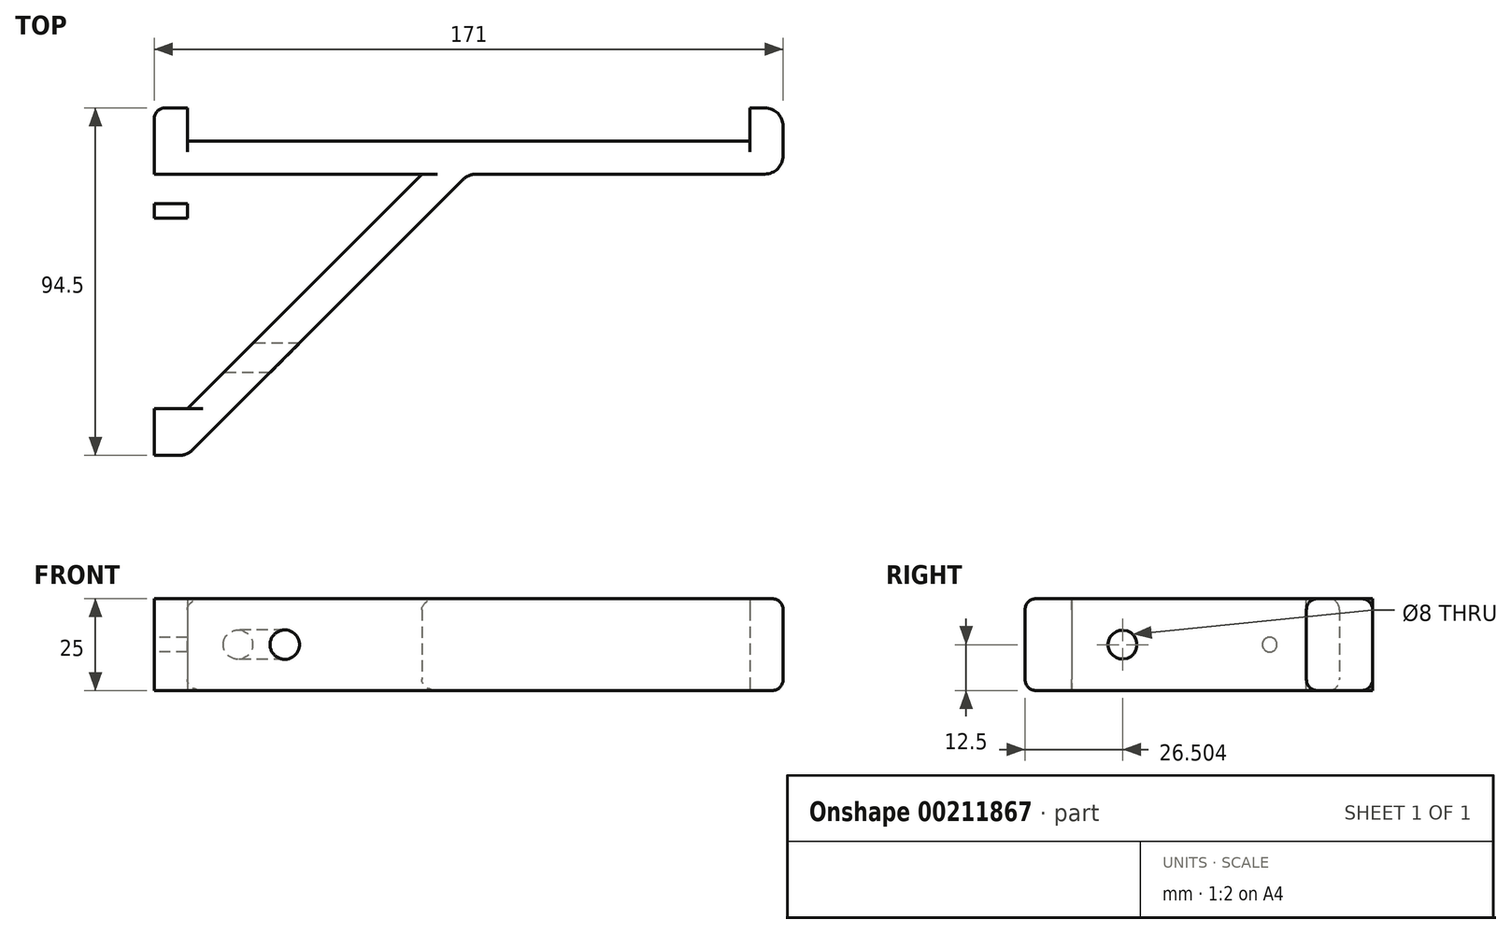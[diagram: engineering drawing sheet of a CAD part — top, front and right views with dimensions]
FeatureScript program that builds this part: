
annotation { "Feature Type Name" : "Feature", "Feature Type Description" : "" }
export const myFeature = defineFeature(function(context is Context, id is Id, definition is map)
    precondition{}
    {
        {
            var Q0;
            Q0=qCreatedBy(makeId("Top.planeOp"),FACE);
            var sketch = newSketch(context, id + "F0", { "sketchPlane" : qUnion([Q0])});
            skLineSegment(sketch, "E0.bottom", {"start": v(-148.67, 15.26) * mm, "end": v(4.33, 15.26) * mm});
            skLineSegment(sketch, "E0.top", {"start": v(-148.67, 24.26) * mm, "end": v(4.33, 24.26) * mm});
            skLineSegment(sketch, "E0.left", {"start": v(-148.67, 15.26) * mm, "end": v(-148.67, 24.26) * mm});
            skLineSegment(sketch, "E0.right", {"start": v(4.33, 15.26) * mm, "end": v(4.33, 24.26) * mm});
            skLineSegment(sketch, "E1.bottom", {"start": v(-148.67, 15.26) * mm, "end": v(-157.67, 15.26) * mm});
            skLineSegment(sketch, "E1.top", {"start": v(-148.67, -61.24) * mm, "end": v(-157.67, -61.24) * mm});
            skLineSegment(sketch, "E1.left", {"start": v(-148.67, -61.24) * mm, "end": v(-148.67, -61.24) * mm});
            skLineSegment(sketch, "E1.right", {"start": v(-157.67, 15.26) * mm, "end": v(-157.67, -61.24) * mm});
            skLineSegment(sketch, "E2", {"start": v(-72.17, 15.26) * mm, "end": v(-72.17, 15.26) * mm});
            skPoint(sketch, "E3.visualSharp", {"position": v(-148.67, 15.26) * mm});
            skLineSegment(sketch, "E4.bottom", {"start": v(-157.67, 15.26) * mm, "end": v(-148.67, 15.26) * mm});
            skLineSegment(sketch, "E4.top", {"start": v(-157.67, 24.26) * mm, "end": v(-148.67, 24.26) * mm});
            skLineSegment(sketch, "E4.left", {"start": v(-157.67, 15.26) * mm, "end": v(-157.67, 24.26) * mm});
            skLineSegment(sketch, "E5", {"start": v(-148.67, 15.26) * mm, "end": v(-148.67, -61.24) * mm});
            skLineSegment(sketch, "E6.bottom", {"start": v(4.33, 15.26) * mm, "end": v(13.33, 15.26) * mm});
            skLineSegment(sketch, "E6.top", {"start": v(4.33, 33.26) * mm, "end": v(13.33, 33.26) * mm});
            skLineSegment(sketch, "E6.left", {"start": v(4.33, 15.26) * mm, "end": v(4.33, 33.26) * mm});
            skLineSegment(sketch, "E6.right", {"start": v(13.33, 15.26) * mm, "end": v(13.33, 33.26) * mm});
            skLineSegment(sketch, "E7.top", {"start": v(-157.67, 33.26) * mm, "end": v(-148.67, 33.26) * mm});
            skLineSegment(sketch, "E7.left", {"start": v(-157.67, 24.26) * mm, "end": v(-157.67, 33.26) * mm});
            skLineSegment(sketch, "E7.right", {"start": v(-148.67, 24.26) * mm, "end": v(-148.67, 33.26) * mm});
            skLineSegment(sketch, "E8", {"start": v(-148.67, -61.24) * mm, "end": v(-72.17, 15.26) * mm});
            skLineSegment(sketch, "E9", {"start": v(-110.42, -22.99) * mm, "end": v(-116.78, -16.62) * mm});
            skLineSegment(sketch, "E10", {"start": v(-116.78, -16.62) * mm, "end": v(-148.67, -48.5) * mm});
            skLineSegment(sketch, "E11", {"start": v(-148.67, -48.5) * mm, "end": v(-116.78, -16.62) * mm});
            skLineSegment(sketch, "E12", {"start": v(-116.78, -16.62) * mm, "end": v(-84.9, 15.26) * mm});
            skSolve(sketch);
        }
        {
            var Q0;
            Q0 = qSketchRegion(id + "F0", true);
            extrude(context, id + "F1", {"entities" : qUnion([Q0]), "depth" : 25 * mm});
        }
        {
            var Q0;
            Q0=makeQuery(id+"F1.opExtrude","SWEPT_FACE",FACE,{"disambiguationData":[OSD([sQuery(id+"F0.wireOp",EDGE,"E1.right"),sQuery(id+"F0.wireOp",EDGE,"E4.left"),sQuery(id+"F0.wireOp",EDGE,"E7.left")])]});
            var sketch = newSketch(context, id + "F2", { "sketchPlane" : qUnion([Q0])});
            skLineSegment(sketch, "E13.0", {"start": v(-15.26, 25) * mm, "end": v(-15.26, 0) * mm});
            skLineSegment(sketch, "E13.1", {"start": v(48.5, 25) * mm, "end": v(48.5, 0) * mm});
            skLineSegment(sketch, "E14", {"start": v(-15.26, 12.5) * mm, "end": v(48.5, 12.5) * mm});
            skCircle(sketch, "E15", {"center": v(-5.26, 12.5) * mm, "radius": 2 * mm});
            skCircle(sketch, "E16", {"center": v(34.74, 12.5) * mm, "radius": 2 * mm});
            skSolve(sketch);
        }
        {
            var Q0;
            {var subQ0=sQuery(id+"F2.wireOp",EDGE,"E15");var subQ1=sQuery(id+"F2.wireOp",EDGE,"E14");var subQ2=makeQuery(id+"F2.imprint","INTERSECT",VERTEX,{"disambiguationData":[OD(0.0)],"derivedFrom":[subQ1,subQ0]});Q0=makeQuery(id+"F2.imprint","IMPRINT",FACE,{"disambiguationData":[TD([[makeQuery(id+"F2.imprint","IMPRINT",EDGE,{"disambiguationData":[TD([[subQ2,-1.0]])],"derivedFrom":subQ1}),1.0]])]});}
            var Q1;
            {var subQ0=sQuery(id+"F2.wireOp",EDGE,"E15");var subQ1=sQuery(id+"F2.wireOp",EDGE,"E14");var subQ2=makeQuery(id+"F2.imprint","INTERSECT",VERTEX,{"disambiguationData":[OD(0.0)],"derivedFrom":[subQ1,subQ0]});Q1=makeQuery(id+"F2.imprint","IMPRINT",FACE,{"disambiguationData":[TD([[makeQuery(id+"F2.imprint","IMPRINT",EDGE,{"disambiguationData":[TD([[subQ2,-1.0]])],"derivedFrom":subQ1}),-1.0]])]});}
            var Q2;
            {var subQ0=sQuery(id+"F2.wireOp",EDGE,"E16");var subQ1=sQuery(id+"F2.wireOp",EDGE,"E14");var subQ2=makeQuery(id+"F2.imprint","INTERSECT",VERTEX,{"disambiguationData":[OD(0.0)],"derivedFrom":[subQ1,subQ0]});Q2=makeQuery(id+"F2.imprint","IMPRINT",FACE,{"disambiguationData":[TD([[makeQuery(id+"F2.imprint","IMPRINT",EDGE,{"disambiguationData":[TD([[subQ2,-1.0]])],"derivedFrom":subQ1}),-1.0]])]});}
            var Q3;
            {var subQ0=sQuery(id+"F2.wireOp",EDGE,"E16");var subQ1=sQuery(id+"F2.wireOp",EDGE,"E14");var subQ2=makeQuery(id+"F2.imprint","INTERSECT",VERTEX,{"disambiguationData":[OD(0.0)],"derivedFrom":[subQ1,subQ0]});Q3=makeQuery(id+"F2.imprint","IMPRINT",FACE,{"disambiguationData":[TD([[makeQuery(id+"F2.imprint","IMPRINT",EDGE,{"disambiguationData":[TD([[subQ2,-1.0]])],"derivedFrom":subQ1}),1.0]])]});}
            extrude(context, id + "F3", {"entities" : qUnion([Q0, Q1, Q2, Q3]), "operationType" : NewBodyOperationType.REMOVE, "endBound" : BoundingType.UP_TO_NEXT, "oppositeDirection" : true, "depth" : 25 * mm});
        }
        {
            var Q0;
            Q0=makeQuery(id+"F1.opExtrude","SWEPT_FACE",FACE,{"disambiguationData":[OSD([sQuery(id+"F0.wireOp",EDGE,"E5")])]});
            var sketch = newSketch(context, id + "F4", { "sketchPlane" : qUnion([Q0])});
            skCircle(sketch, "E17", {"center": v(5.26, 12.5) * mm, "radius": 4 * mm});
            skCircle(sketch, "E18", {"center": v(-34.74, 12.5) * mm, "radius": 4 * mm});
            skSolve(sketch);
        }
        {
            var Q0;
            Q0=makeQuery(id+"F4.imprint","IMPRINT",FACE,{"disambiguationData":[TD([[makeQuery(id+"F4.imprint","IMPRINT",EDGE,{"derivedFrom":makeQuery(id+"F3.boolean.opBoolean","COPY",EDGE,{"derivedFrom":makeQuery(id+"F3.opExtrude","CAP_EDGE",EDGE,{"disambiguationData":[OSD([sQuery(id+"F2.wireOp",EDGE,"E15")])],"isStart":false})})}),-1.0]])]});
            var Q1;
            Q1=makeQuery(id+"F4.imprint","IMPRINT",FACE,{"disambiguationData":[TD([[makeQuery(id+"F4.imprint","IMPRINT",EDGE,{"derivedFrom":makeQuery(id+"F3.boolean.opBoolean","COPY",EDGE,{"derivedFrom":makeQuery(id+"F3.opExtrude","CAP_EDGE",EDGE,{"disambiguationData":[OSD([sQuery(id+"F2.wireOp",EDGE,"E16")])],"isStart":false})})}),-1.0]])]});
            var Q2;
            Q2=makeQuery(id+"F4.imprint","IMPRINT",FACE,{"disambiguationData":[TD([[makeQuery(id+"F4.imprint","IMPRINT",EDGE,{"derivedFrom":sQuery(id+"F4.wireOp",EDGE,"E18")}),1.0]])]});
            var Q3;
            Q3=makeQuery(id+"F4.imprint","IMPRINT",FACE,{"disambiguationData":[TD([[makeQuery(id+"F4.imprint","IMPRINT",EDGE,{"derivedFrom":sQuery(id+"F4.wireOp",EDGE,"E17")}),1.0]])]});
            extrude(context, id + "F5", {"entities" : qUnion([Q0, Q1, Q2, Q3]), "operationType" : NewBodyOperationType.REMOVE, "oppositeDirection" : true, "depth" : 4 * mm});
        }
        {
            var Q0;
            Q0=makeQuery(id+"F4.imprint","IMPRINT",FACE,{"disambiguationData":[TD([[makeQuery(id+"F4.imprint","IMPRINT",EDGE,{"derivedFrom":sQuery(id+"F4.wireOp",EDGE,"E18")}),1.0]])]});
            var Q1;
            Q1=makeQuery(id+"F4.imprint","IMPRINT",FACE,{"disambiguationData":[TD([[makeQuery(id+"F4.imprint","IMPRINT",EDGE,{"derivedFrom":makeQuery(id+"F3.boolean.opBoolean","COPY",EDGE,{"derivedFrom":makeQuery(id+"F3.opExtrude","CAP_EDGE",EDGE,{"disambiguationData":[OSD([sQuery(id+"F2.wireOp",EDGE,"E16")])],"isStart":false})})}),-1.0]])]});
            extrude(context, id + "F6", {"entities" : qUnion([Q0, Q1]), "operationType" : NewBodyOperationType.REMOVE, "endBound" : BoundingType.THROUGH_ALL, "depth" : 80.63 * mm});
        }
        {
            var Q0;
            Q0=makeQuery(id+"F1.opExtrude","SWEPT_EDGE",EDGE,{"disambiguationData":[OSD([sQuery(id+"F0.wireOp",EDGE,"E1.top"),sQuery(id+"F0.wireOp",EDGE,"E5"),sQuery(id+"F0.wireOp",EDGE,"E8")])]});
            fillet(context, id + "F7", {"entities" : qUnion([Q0]), "radius" : 5 * mm, "tangentPropagation" : true, "allowEdgeOverflow" : false});
        }
        {
            var Q0;
            Q0=makeQuery(id+"F1.opExtrude","SWEPT_EDGE",EDGE,{"disambiguationData":[OSD([sQuery(id+"F0.wireOp",EDGE,"E0.bottom"),sQuery(id+"F0.wireOp",EDGE,"E8")])]});
            fillet(context, id + "F8", {"entities" : qUnion([Q0]), "radius" : 5 * mm, "tangentPropagation" : true, "allowEdgeOverflow" : false});
        }
        {
            var Q0;
            Q0=makeQuery(id+"F1.opExtrude","SWEPT_EDGE",EDGE,{"disambiguationData":[OSD([sQuery(id+"F0.wireOp",EDGE,"E6.bottom"),sQuery(id+"F0.wireOp",EDGE,"E6.right")])]});
            fillet(context, id + "F9", {"entities" : qUnion([Q0]), "radius" : 5 * mm, "tangentPropagation" : true, "allowEdgeOverflow" : false});
        }
        {
            var Q0;
            Q0=makeQuery(id+"F1.opExtrude","SWEPT_EDGE",EDGE,{"disambiguationData":[OSD([sQuery(id+"F0.wireOp",EDGE,"E6.top"),sQuery(id+"F0.wireOp",EDGE,"E6.right")])]});
            fillet(context, id + "F10", {"entities" : qUnion([Q0]), "radius" : 5 * mm, "tangentPropagation" : true, "allowEdgeOverflow" : false});
        }
        {
            var Q0;
            Q0=makeQuery(id+"F1.opExtrude","SWEPT_EDGE",EDGE,{"disambiguationData":[OSD([sQuery(id+"F0.wireOp",EDGE,"E7.top"),sQuery(id+"F0.wireOp",EDGE,"E7.left")])]});
            var Q1;
            Q1=makeQuery(id+"F1.opExtrude","CAP_EDGE",EDGE,{"disambiguationData":[OSD([sQuery(id+"F0.wireOp",EDGE,"E0.bottom"),sQuery(id+"F0.wireOp",EDGE,"E6.bottom")])],"isStart":false});
            var Q2;
            Q2=makeQuery(id+"F1.opExtrude","CAP_EDGE",EDGE,{"disambiguationData":[OSD([sQuery(id+"F0.wireOp",EDGE,"E0.bottom")])],"isStart":false});
            var Q3;
            Q3=makeQuery(id+"F1.opExtrude","CAP_EDGE",EDGE,{"disambiguationData":[OSD([sQuery(id+"F0.wireOp",EDGE,"E11"),sQuery(id+"F0.wireOp",EDGE,"E12")])],"isStart":false});
            var Q4;
            Q4=makeQuery(id+"F1.opExtrude","CAP_EDGE",EDGE,{"disambiguationData":[OSD([sQuery(id+"F0.wireOp",EDGE,"E5")])],"isStart":false});
            var Q5;
            Q5=makeQuery(id+"F1.opExtrude","CAP_EDGE",EDGE,{"disambiguationData":[OSD([sQuery(id+"F0.wireOp",EDGE,"E0.top")])],"isStart":false});
            fillet(context, id + "F11", {"entities" : qUnion([Q0, Q1, Q2, Q3, Q4, Q5]), "radius" : 3 * mm, "tangentPropagation" : true, "allowEdgeOverflow" : false});
        }
        {
            var Q0;
            Q0=makeQuery(id+"F1.opExtrude","CAP_EDGE",EDGE,{"disambiguationData":[OSD([sQuery(id+"F0.wireOp",EDGE,"E0.bottom"),sQuery(id+"F0.wireOp",EDGE,"E6.bottom")])],"isStart":true});
            var Q1;
            Q1=makeQuery(id+"F1.opExtrude","CAP_EDGE",EDGE,{"disambiguationData":[OSD([sQuery(id+"F0.wireOp",EDGE,"E8")])],"isStart":true});
            var Q2;
            Q2=makeQuery(id+"F1.opExtrude","CAP_EDGE",EDGE,{"disambiguationData":[OSD([sQuery(id+"F0.wireOp",EDGE,"E0.bottom")])],"isStart":true});
            var Q3;
            Q3=makeQuery(id+"F1.opExtrude","CAP_EDGE",EDGE,{"disambiguationData":[OSD([sQuery(id+"F0.wireOp",EDGE,"E11"),sQuery(id+"F0.wireOp",EDGE,"E12")])],"isStart":true});
            var Q4;
            Q4=makeQuery(id+"F1.opExtrude","CAP_EDGE",EDGE,{"disambiguationData":[OSD([sQuery(id+"F0.wireOp",EDGE,"E5")])],"isStart":true});
            var Q5;
            Q5=makeQuery(id+"F1.opExtrude","CAP_EDGE",EDGE,{"disambiguationData":[OSD([sQuery(id+"F0.wireOp",EDGE,"E0.top")])],"isStart":true});
            fillet(context, id + "F12", {"entities" : qUnion([Q0, Q1, Q2, Q3, Q4, Q5]), "radius" : 3 * mm, "tangentPropagation" : true, "allowEdgeOverflow" : false});
        }
    });
